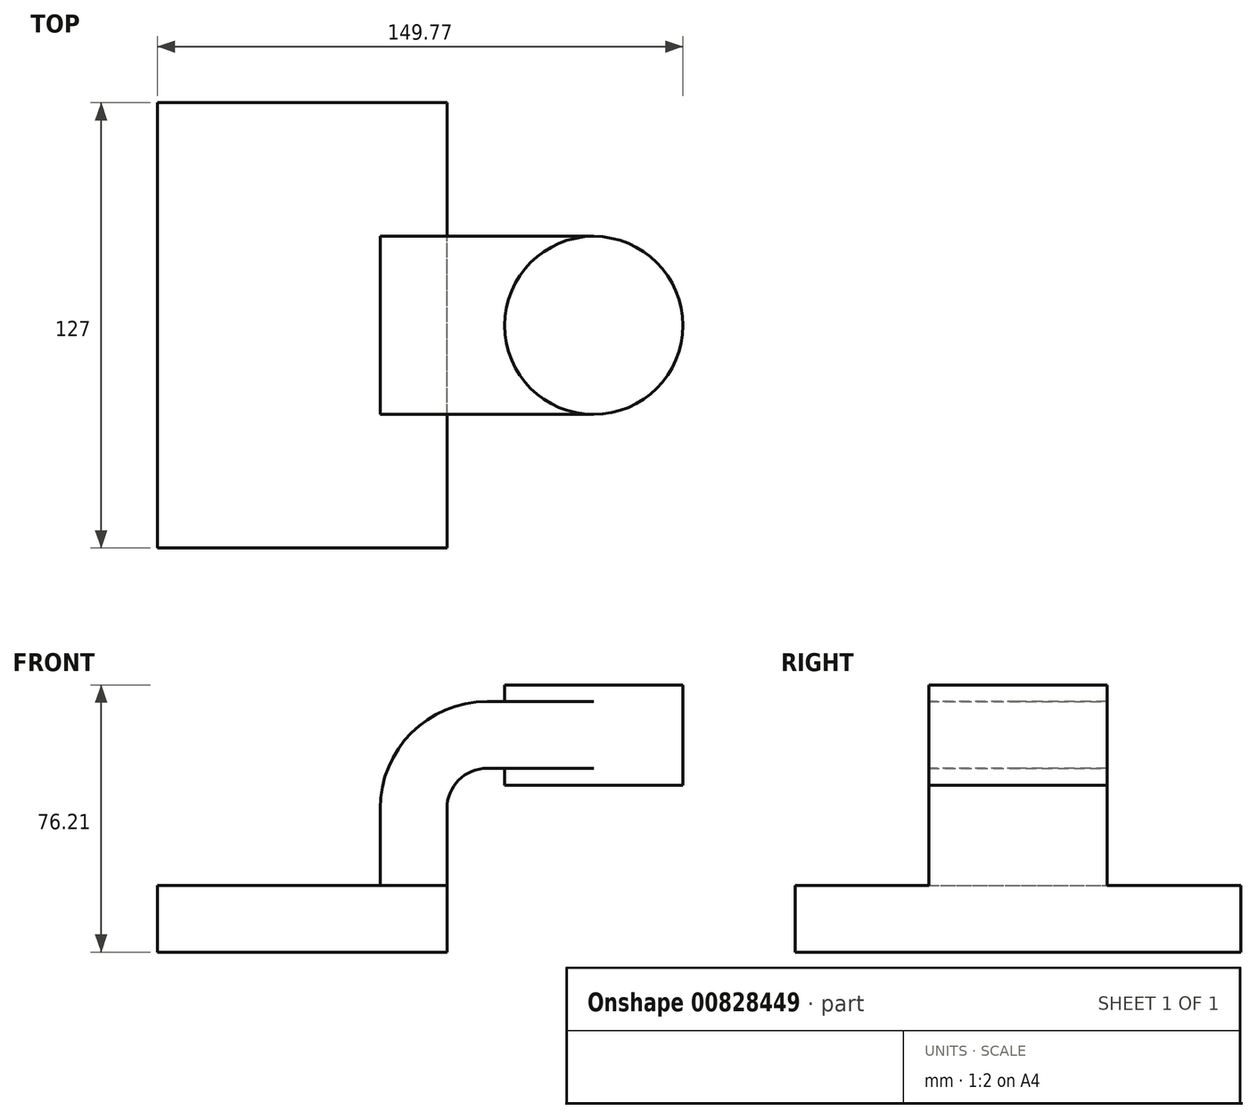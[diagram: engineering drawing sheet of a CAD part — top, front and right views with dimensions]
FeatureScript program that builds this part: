
annotation { "Feature Type Name" : "Feature", "Feature Type Description" : "" }
export const myFeature = defineFeature(function(context is Context, id is Id, definition is map)
    precondition{}
    {
        {
            var Q0;
            Q0=qCreatedBy(makeId("Front.planeOp"),FACE);
            var sketch = newSketch(context, id + "F0", { "sketchPlane" : qUnion([Q0])});
            skLineSegment(sketch, "E0.bottom", {"start": v(41.28, -9.52) * mm, "end": v(-41.28, -9.53) * mm});
            skLineSegment(sketch, "E0.top", {"start": v(41.28, 9.53) * mm, "end": v(-41.28, 9.53) * mm});
            skLineSegment(sketch, "E0.left", {"start": v(41.28, -9.52) * mm, "end": v(41.28, 9.53) * mm});
            skLineSegment(sketch, "E0.right", {"start": v(-41.28, -9.53) * mm, "end": v(-41.28, 9.53) * mm});
            skPoint(sketch, "E0.middle", {"position": v(0, 0) * mm});
            skLineSegment(sketch, "E1.bottom", {"start": v(108.49, 38.1) * mm, "end": v(57.69, 38.1) * mm});
            skLineSegment(sketch, "E1.top", {"start": v(108.49, 66.68) * mm, "end": v(57.69, 66.68) * mm});
            skLineSegment(sketch, "E1.left", {"start": v(108.49, 38.1) * mm, "end": v(108.49, 66.68) * mm});
            skLineSegment(sketch, "E1.right", {"start": v(57.69, 38.1) * mm, "end": v(57.69, 66.68) * mm});
            skPoint(sketch, "E1.middle", {"position": v(83.09, 52.39) * mm});
            skLineSegment(sketch, "E2", {"start": v(41.28, 9.53) * mm, "end": v(41.28, 31.43) * mm});
            skArc(sketch, "E3", {"start": v(41.28, 31.43) * mm, "mid": v(44.63, 39.52) * mm, "end": v(52.72, 42.88) * mm});
            skLineSegment(sketch, "E4", {"start": v(52.72, 42.88) * mm, "end": v(83.09, 42.88) * mm});
            skLineSegment(sketch, "E5.0", {"start": v(52.72, 61.93) * mm, "end": v(83.09, 61.93) * mm});
            skArc(sketch, "E5.1", {"start": v(22.23, 31.43) * mm, "mid": v(31.16, 53) * mm, "end": v(52.72, 61.93) * mm});
            skLineSegment(sketch, "E5.2", {"start": v(22.22, 9.53) * mm, "end": v(22.22, 31.43) * mm});
            skLineSegment(sketch, "E6", {"start": v(83.09, 42.88) * mm, "end": v(83.09, 38.1) * mm});
            skLineSegment(sketch, "E7", {"start": v(83.09, 38.1) * mm, "end": v(83.09, 61.93) * mm});
            skLineSegment(sketch, "E8", {"start": v(83.09, 61.93) * mm, "end": v(83.09, 66.68) * mm});
            skFitSpline(sketch, "E9", {"points": [v(-41.28, 9.52) * mm, v(52.72, 61.93) * mm], "startDerivative": vector(-1.33, 115.94) * mm, "endDerivative": vector(107.05, -17.89) * mm});
            skSolve(sketch);
        }
        {
            var Q0;
            Q0=makeQuery(id+"F0.imprint","IMPRINT",FACE,{"disambiguationData":[TD([[makeQuery(id+"F0.imprint","IMPRINT",EDGE,{"derivedFrom":sQuery(id+"F0.wireOp",EDGE,"E0.bottom")}),-1.0]])]});
            extrude(context, id + "F1", {"entities" : qUnion([Q0]), "endBound" : BoundingType.SYMMETRIC, "depth" : 127 * mm, "offsetDistance" : 25.4 * mm});
        }
        {
            var Q0;
            {var subQ1=sQuery(id+"F0.wireOp",EDGE,"E2");Q0=makeQuery(id+"F0.imprint","IMPRINT",FACE,{"disambiguationData":[TD([[makeQuery(id+"F0.imprint","IMPRINT",EDGE,{"derivedFrom":subQ1}),1.0]])]});}
            var Q1;
            {var subQ0=sQuery(id+"F0.wireOp",EDGE,"E4");var subQ1=sQuery(id+"F0.wireOp",EDGE,"E1.right");var subQ2=makeQuery(id+"F0.imprint","INTERSECT",VERTEX,{"derivedFrom":[subQ1,subQ0]});Q1=makeQuery(id+"F0.imprint","IMPRINT",FACE,{"disambiguationData":[TD([[makeQuery(id+"F0.imprint","IMPRINT",EDGE,{"disambiguationData":[TD([[subQ2,-1.0]])],"derivedFrom":subQ1}),-1.0]])]});}
            extrude(context, id + "F2", {"entities" : qUnion([Q0, Q1]), "operationType" : NewBodyOperationType.ADD, "endBound" : BoundingType.SYMMETRIC, "depth" : 50.8 * mm, "offsetDistance" : 25.4 * mm});
        }
        {
            var Q0;
            Q0=makeQuery(id+"F0.imprint","IMPRINT",FACE,{"disambiguationData":[TD([[makeQuery(id+"F0.imprint","IMPRINT",EDGE,{"derivedFrom":sQuery(id+"F0.wireOp",EDGE,"E5.1")}),1.0]])]});
            extrude(context, id + "F3", {"entities" : qUnion([Q0]), "operationType" : NewBodyOperationType.ADD, "endBound" : BoundingType.SYMMETRIC, "depth" : 15.88 * mm, "offsetDistance" : 25.4 * mm});
        }
        {
            var Q0;
            {var subQ4=sQuery(id+"F0.wireOp",EDGE,"E1.left");Q0=makeQuery(id+"F0.imprint","IMPRINT",FACE,{"disambiguationData":[TD([[makeQuery(id+"F0.imprint","IMPRINT",EDGE,{"derivedFrom":subQ4}),1.0]])]});}
            var Q1;
            Q1=sQuery(id+"F0.wireOp",EDGE,"E7");
            revolve(context, id + "F4", {"operationType" : NewBodyOperationType.ADD, "surfaceOperationType" : NewSurfaceOperationType.NEW, "entities" : qUnion([Q0]), "axis" : qUnion([Q1]), "revolveType" : RevolveType.FULL});
        }
    });
